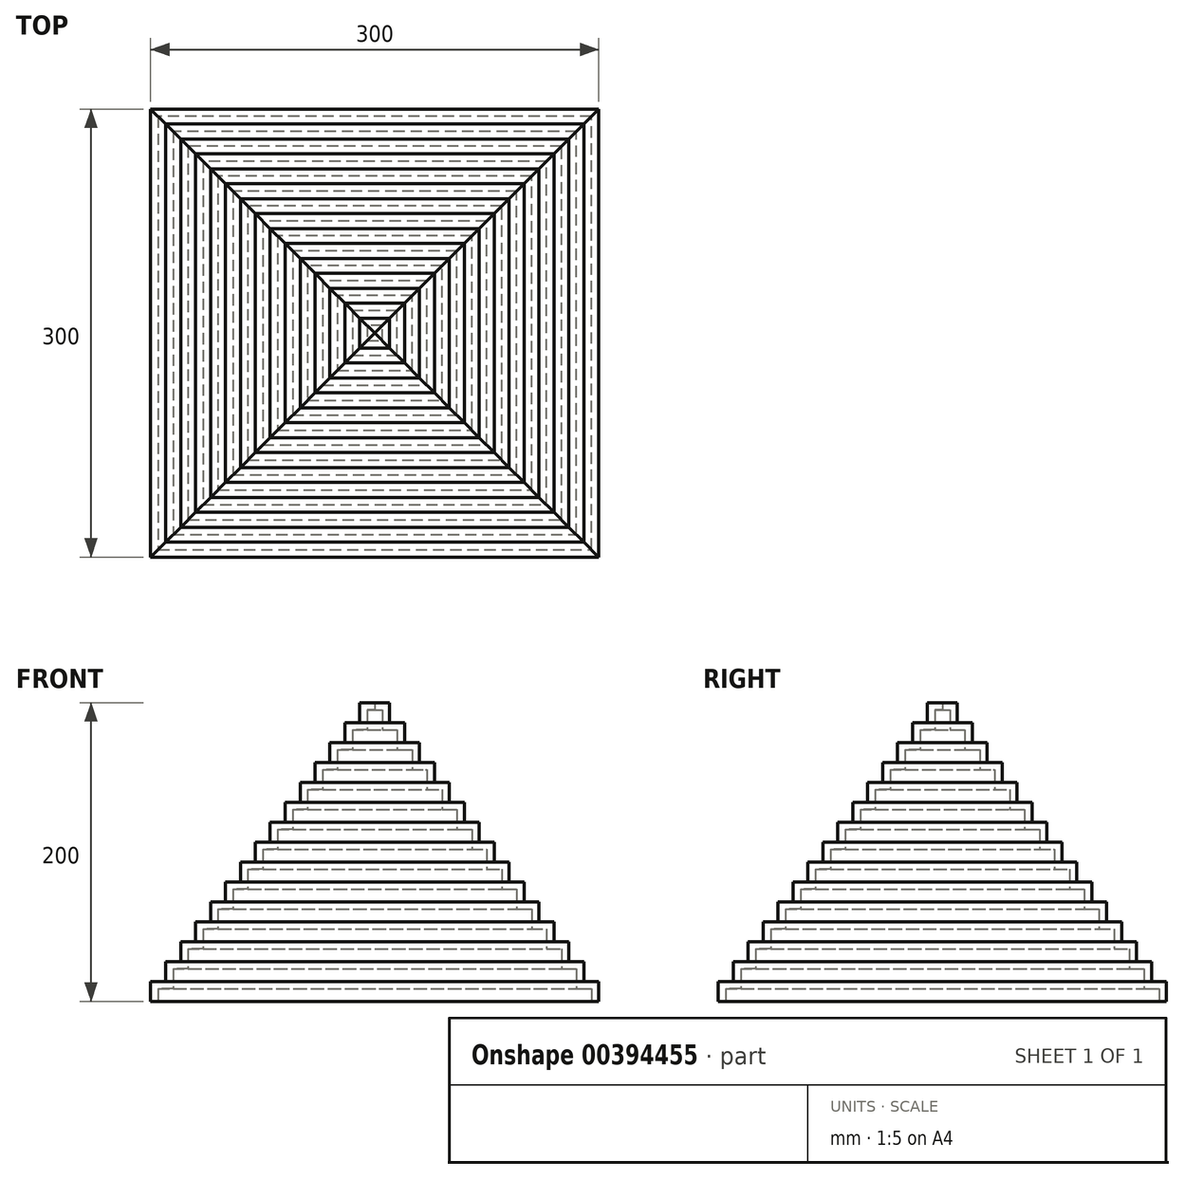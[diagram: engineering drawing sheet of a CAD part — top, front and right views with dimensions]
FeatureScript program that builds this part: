
annotation { "Feature Type Name" : "Feature", "Feature Type Description" : "" }
export const myFeature = defineFeature(function(context is Context, id is Id, definition is map)
    precondition{}
    {
        {
            var Q0;
            Q0=qCreatedBy(makeId("Front.planeOp"),FACE);
            var sketch = newSketch(context, id + "F0", { "sketchPlane" : qUnion([Q0])});
            skLineSegment(sketch, "E0", {"start": v(-150, 0) * mm, "end": v(150, 0) * mm, "construction": true});
            skLineSegment(sketch, "E1", {"start": v(150, 0) * mm, "end": v(150, 13.33) * mm});
            skLineSegment(sketch, "E2", {"start": v(150, 13.33) * mm, "end": v(140, 13.33) * mm});
            skLineSegment(sketch, "E3", {"start": v(140, 13.33) * mm, "end": v(140, 26.67) * mm});
            skLineSegment(sketch, "E4", {"start": v(140, 26.67) * mm, "end": v(130, 26.67) * mm});
            skLineSegment(sketch, "E5", {"start": v(130, 26.67) * mm, "end": v(130, 40) * mm});
            skLineSegment(sketch, "E6", {"start": v(130, 40) * mm, "end": v(120, 40) * mm});
            skLineSegment(sketch, "E7", {"start": v(120, 40) * mm, "end": v(120, 53.33) * mm});
            skLineSegment(sketch, "E8", {"start": v(120, 53.33) * mm, "end": v(110, 53.33) * mm});
            skLineSegment(sketch, "E9", {"start": v(110, 53.33) * mm, "end": v(110, 66.67) * mm});
            skLineSegment(sketch, "E10", {"start": v(110, 66.67) * mm, "end": v(100, 66.67) * mm});
            skLineSegment(sketch, "E11", {"start": v(100, 66.67) * mm, "end": v(100, 80) * mm});
            skLineSegment(sketch, "E12", {"start": v(100, 80) * mm, "end": v(90, 80) * mm});
            skLineSegment(sketch, "E13", {"start": v(90, 80) * mm, "end": v(90, 93.33) * mm});
            skLineSegment(sketch, "E14", {"start": v(90, 93.33) * mm, "end": v(80, 93.33) * mm});
            skLineSegment(sketch, "E15", {"start": v(80, 93.33) * mm, "end": v(80, 106.67) * mm});
            skLineSegment(sketch, "E16", {"start": v(80, 106.67) * mm, "end": v(70, 106.67) * mm});
            skLineSegment(sketch, "E17", {"start": v(70, 106.67) * mm, "end": v(70, 120) * mm});
            skLineSegment(sketch, "E18", {"start": v(70, 120) * mm, "end": v(60, 120) * mm});
            skLineSegment(sketch, "E19", {"start": v(60, 120) * mm, "end": v(60, 133.33) * mm});
            skLineSegment(sketch, "E20", {"start": v(60, 133.33) * mm, "end": v(50, 133.33) * mm});
            skLineSegment(sketch, "E21", {"start": v(50, 133.33) * mm, "end": v(50, 146.67) * mm});
            skLineSegment(sketch, "E22", {"start": v(50, 146.67) * mm, "end": v(40, 146.67) * mm});
            skLineSegment(sketch, "E23", {"start": v(40, 146.67) * mm, "end": v(40, 160) * mm});
            skLineSegment(sketch, "E24", {"start": v(40, 160) * mm, "end": v(30, 160) * mm});
            skLineSegment(sketch, "E25", {"start": v(30, 160) * mm, "end": v(30, 173.33) * mm});
            skLineSegment(sketch, "E26", {"start": v(30, 173.33) * mm, "end": v(20, 173.33) * mm});
            skLineSegment(sketch, "E27", {"start": v(20, 173.33) * mm, "end": v(20, 186.67) * mm});
            skLineSegment(sketch, "E28", {"start": v(20, 186.67) * mm, "end": v(10, 186.67) * mm});
            skLineSegment(sketch, "E29", {"start": v(10, 186.67) * mm, "end": v(10, 200) * mm});
            skLineSegment(sketch, "E30", {"start": v(10, 200) * mm, "end": v(0, 200) * mm});
            skLineSegment(sketch, "E31", {"start": v(0, 0) * mm, "end": v(0, 87.04) * mm, "construction": true});
            skLineSegment(sketch, "E32.0", {"start": v(5, 195) * mm, "end": v(0, 195) * mm});
            skLineSegment(sketch, "E32.1", {"start": v(5, 181.67) * mm, "end": v(5, 195) * mm});
            skLineSegment(sketch, "E32.2", {"start": v(15, 181.67) * mm, "end": v(5, 181.67) * mm});
            skLineSegment(sketch, "E32.3", {"start": v(15, 168.33) * mm, "end": v(15, 181.67) * mm});
            skLineSegment(sketch, "E32.4", {"start": v(25, 168.33) * mm, "end": v(15, 168.33) * mm});
            skLineSegment(sketch, "E32.5", {"start": v(25, 155) * mm, "end": v(25, 168.33) * mm});
            skLineSegment(sketch, "E32.6", {"start": v(35, 155) * mm, "end": v(25, 155) * mm});
            skLineSegment(sketch, "E32.7", {"start": v(35, 141.67) * mm, "end": v(35, 155) * mm});
            skLineSegment(sketch, "E32.8", {"start": v(105, 61.67) * mm, "end": v(95, 61.67) * mm});
            skLineSegment(sketch, "E32.9", {"start": v(105, 48.33) * mm, "end": v(105, 61.67) * mm});
            skLineSegment(sketch, "E32.10", {"start": v(115, 48.33) * mm, "end": v(105, 48.33) * mm});
            skLineSegment(sketch, "E32.11", {"start": v(115, 35) * mm, "end": v(115, 48.33) * mm});
            skLineSegment(sketch, "E32.12", {"start": v(125, 35) * mm, "end": v(115, 35) * mm});
            skLineSegment(sketch, "E32.13", {"start": v(125, 21.67) * mm, "end": v(125, 35) * mm});
            skLineSegment(sketch, "E32.14", {"start": v(145, 0) * mm, "end": v(145, 8.33) * mm});
            skLineSegment(sketch, "E32.15", {"start": v(145, 8.33) * mm, "end": v(135, 8.33) * mm});
            skLineSegment(sketch, "E32.16", {"start": v(135, 8.33) * mm, "end": v(135, 21.67) * mm});
            skLineSegment(sketch, "E32.17", {"start": v(135, 21.67) * mm, "end": v(125, 21.67) * mm});
            skLineSegment(sketch, "E32.18", {"start": v(95, 61.67) * mm, "end": v(95, 75) * mm});
            skLineSegment(sketch, "E32.19", {"start": v(95, 75) * mm, "end": v(85, 75) * mm});
            skLineSegment(sketch, "E32.20", {"start": v(85, 75) * mm, "end": v(85, 88.33) * mm});
            skLineSegment(sketch, "E32.21", {"start": v(85, 88.33) * mm, "end": v(75, 88.33) * mm});
            skLineSegment(sketch, "E32.22", {"start": v(75, 88.33) * mm, "end": v(75, 101.67) * mm});
            skLineSegment(sketch, "E32.23", {"start": v(75, 101.67) * mm, "end": v(65, 101.67) * mm});
            skLineSegment(sketch, "E32.24", {"start": v(65, 101.67) * mm, "end": v(65, 115) * mm});
            skLineSegment(sketch, "E32.25", {"start": v(65, 115) * mm, "end": v(55, 115) * mm});
            skLineSegment(sketch, "E32.26", {"start": v(55, 115) * mm, "end": v(55, 128.33) * mm});
            skLineSegment(sketch, "E32.27", {"start": v(55, 128.33) * mm, "end": v(45, 128.33) * mm});
            skLineSegment(sketch, "E32.28", {"start": v(45, 128.33) * mm, "end": v(45, 141.67) * mm});
            skLineSegment(sketch, "E32.29", {"start": v(45, 141.67) * mm, "end": v(35, 141.67) * mm});
            skLineSegment(sketch, "E33", {"start": v(145, 0) * mm, "end": v(150, 0) * mm});
            skLineSegment(sketch, "E34", {"start": v(0, 200) * mm, "end": v(0, 195) * mm});
            skSolve(sketch);
        }
        {
            var Q0;
            Q0=qSketchRegion(id+"F0",true);
            extrude(context, id + "F1", {"entities" : qUnion([Q0]), "depth" : 150 * mm, "hasSecondDirection" : true, "secondDirectionOppositeDirection" : true, "secondDirectionDepth" : 150 * mm});
        }
        {
            var Q0;
            Q0=qCreatedBy(makeId("Right.planeOp"),FACE);
            var sketch = newSketch(context, id + "F2", { "sketchPlane" : qUnion([Q0])});
            skLineSegment(sketch, "E35", {"start": v(-150, 0) * mm, "end": v(150, 0) * mm, "construction": true});
            skLineSegment(sketch, "E36", {"start": v(0, 0) * mm, "end": v(0, 200) * mm});
            skLineSegment(sketch, "E37", {"start": v(150, 0) * mm, "end": v(150, 13.33) * mm});
            skSolve(sketch);
        }
        {
            var Q0;
            Q0=qCreatedBy(makeId("Right.planeOp"),FACE);
            var Q1;
            Q1=sQuery(id+"F2.wireOp",EDGE,"E36");
            cPlane(context, id + "F3", {"entities" : qUnion([Q0, Q1]), "cplaneType" : CPlaneType.LINE_ANGLE, "offset" : 47 * mm, "angle" : 45 * degree, "oppositeDirection" : true, "width" : 150 * mm, "height" : 150 * mm});
        }
        {
            var Q0;
            Q0=qCreatedBy(id+"F3.planeOp",FACE);
            var sketch = newSketch(context, id + "F4", { "sketchPlane" : qUnion([Q0])});
            skLineSegment(sketch, "E38.bottom", {"start": v(136.08, 226.9) * mm, "end": v(0, 226.9) * mm});
            skLineSegment(sketch, "E38.top", {"start": v(136.08, -11.6) * mm, "end": v(0, -11.6) * mm});
            skLineSegment(sketch, "E38.left", {"start": v(136.08, 226.9) * mm, "end": v(136.08, -11.6) * mm});
            skLineSegment(sketch, "E38.right", {"start": v(0, 226.9) * mm, "end": v(0, -11.6) * mm});
            skSolve(sketch);
        }
        {
            var Q0;
            Q0=qSketchRegion(id+"F4",true);
            extrude(context, id + "F5", {"entities" : qUnion([Q0]), "operationType" : NewBodyOperationType.REMOVE, "endBound" : BoundingType.THROUGH_ALL, "oppositeDirection" : true, "depth" : 25 * mm});
        }
        {
            var Q0;
            Q0=qCreatedBy(makeId("Right.planeOp"),FACE);
            var Q1;
            Q1=sQuery(id+"F2.wireOp",EDGE,"E36");
            cPlane(context, id + "F6", {"entities" : qUnion([Q0, Q1]), "cplaneType" : CPlaneType.LINE_ANGLE, "offset" : 25 * mm, "angle" : 45 * degree, "width" : 150 * mm, "height" : 150 * mm});
        }
        {
            var Q0;
            Q0=qCreatedBy(id+"F6.planeOp",FACE);
            var sketch = newSketch(context, id + "F7", { "sketchPlane" : qUnion([Q0])});
            skLineSegment(sketch, "E39.bottom", {"start": v(-211.06, 218.4) * mm, "end": v(0, 218.4) * mm});
            skLineSegment(sketch, "E39.top", {"start": v(-211.06, -13.72) * mm, "end": v(0, -13.72) * mm});
            skLineSegment(sketch, "E39.left", {"start": v(-211.06, 218.4) * mm, "end": v(-211.06, -13.72) * mm});
            skLineSegment(sketch, "E39.right", {"start": v(0, 218.4) * mm, "end": v(0, -13.72) * mm});
            skSolve(sketch);
        }
        {
            var Q0;
            Q0=qSketchRegion(id+"F7",true);
            extrude(context, id + "F8", {"entities" : qUnion([Q0]), "operationType" : NewBodyOperationType.REMOVE, "endBound" : BoundingType.THROUGH_ALL, "oppositeDirection" : true, "depth" : 25 * mm});
        }
        {
            var Q0;
            Q0=makeQuery(id+"F1.opExtrude","SWEPT_BODY",BODY,{"disambiguationData":[OSD([sQuery(id+"F0.wireOp",EDGE,"E1"),sQuery(id+"F0.wireOp",EDGE,"E2"),sQuery(id+"F0.wireOp",EDGE,"E3"),sQuery(id+"F0.wireOp",EDGE,"E4"),sQuery(id+"F0.wireOp",EDGE,"E5"),sQuery(id+"F0.wireOp",EDGE,"E6"),sQuery(id+"F0.wireOp",EDGE,"E7"),sQuery(id+"F0.wireOp",EDGE,"E8"),sQuery(id+"F0.wireOp",EDGE,"E9"),sQuery(id+"F0.wireOp",EDGE,"E10"),sQuery(id+"F0.wireOp",EDGE,"E11"),sQuery(id+"F0.wireOp",EDGE,"E12"),sQuery(id+"F0.wireOp",EDGE,"E13"),sQuery(id+"F0.wireOp",EDGE,"E14"),sQuery(id+"F0.wireOp",EDGE,"E15"),sQuery(id+"F0.wireOp",EDGE,"E16"),sQuery(id+"F0.wireOp",EDGE,"E17"),sQuery(id+"F0.wireOp",EDGE,"E18"),sQuery(id+"F0.wireOp",EDGE,"E19"),sQuery(id+"F0.wireOp",EDGE,"E20"),sQuery(id+"F0.wireOp",EDGE,"E21"),sQuery(id+"F0.wireOp",EDGE,"E22"),sQuery(id+"F0.wireOp",EDGE,"E23"),sQuery(id+"F0.wireOp",EDGE,"E24"),sQuery(id+"F0.wireOp",EDGE,"E25"),sQuery(id+"F0.wireOp",EDGE,"E26"),sQuery(id+"F0.wireOp",EDGE,"E27"),sQuery(id+"F0.wireOp",EDGE,"E28"),sQuery(id+"F0.wireOp",EDGE,"E29"),sQuery(id+"F0.wireOp",EDGE,"E30"),sQuery(id+"F0.wireOp",EDGE,"E32.0"),sQuery(id+"F0.wireOp",EDGE,"E32.1"),sQuery(id+"F0.wireOp",EDGE,"E32.2"),sQuery(id+"F0.wireOp",EDGE,"E32.3"),sQuery(id+"F0.wireOp",EDGE,"E32.4"),sQuery(id+"F0.wireOp",EDGE,"E32.5"),sQuery(id+"F0.wireOp",EDGE,"E32.6"),sQuery(id+"F0.wireOp",EDGE,"E32.7"),sQuery(id+"F0.wireOp",EDGE,"E32.8"),sQuery(id+"F0.wireOp",EDGE,"E32.9"),sQuery(id+"F0.wireOp",EDGE,"E32.10"),sQuery(id+"F0.wireOp",EDGE,"E32.11"),sQuery(id+"F0.wireOp",EDGE,"E32.12"),sQuery(id+"F0.wireOp",EDGE,"E32.13"),sQuery(id+"F0.wireOp",EDGE,"E32.14"),sQuery(id+"F0.wireOp",EDGE,"E32.15"),sQuery(id+"F0.wireOp",EDGE,"E32.16"),sQuery(id+"F0.wireOp",EDGE,"E32.17"),sQuery(id+"F0.wireOp",EDGE,"E32.18"),sQuery(id+"F0.wireOp",EDGE,"E32.19"),sQuery(id+"F0.wireOp",EDGE,"E32.20"),sQuery(id+"F0.wireOp",EDGE,"E32.21"),sQuery(id+"F0.wireOp",EDGE,"E32.22"),sQuery(id+"F0.wireOp",EDGE,"E32.23"),sQuery(id+"F0.wireOp",EDGE,"E32.24"),sQuery(id+"F0.wireOp",EDGE,"E32.25"),sQuery(id+"F0.wireOp",EDGE,"E32.26"),sQuery(id+"F0.wireOp",EDGE,"E32.27"),sQuery(id+"F0.wireOp",EDGE,"E32.28"),sQuery(id+"F0.wireOp",EDGE,"E32.29"),sQuery(id+"F0.wireOp",EDGE,"E33"),sQuery(id+"F0.wireOp",EDGE,"E34")])]});
            var Q1;
            Q1=sQuery(id+"F2.wireOp",EDGE,"E36");
            circularPattern(context, id + "F9", {"entities" : qUnion([Q0]), "axis" : qUnion([Q1]), "angle" : 360 * degree, "instanceCount" : 4, "equalSpace" : true});
        }
    });
